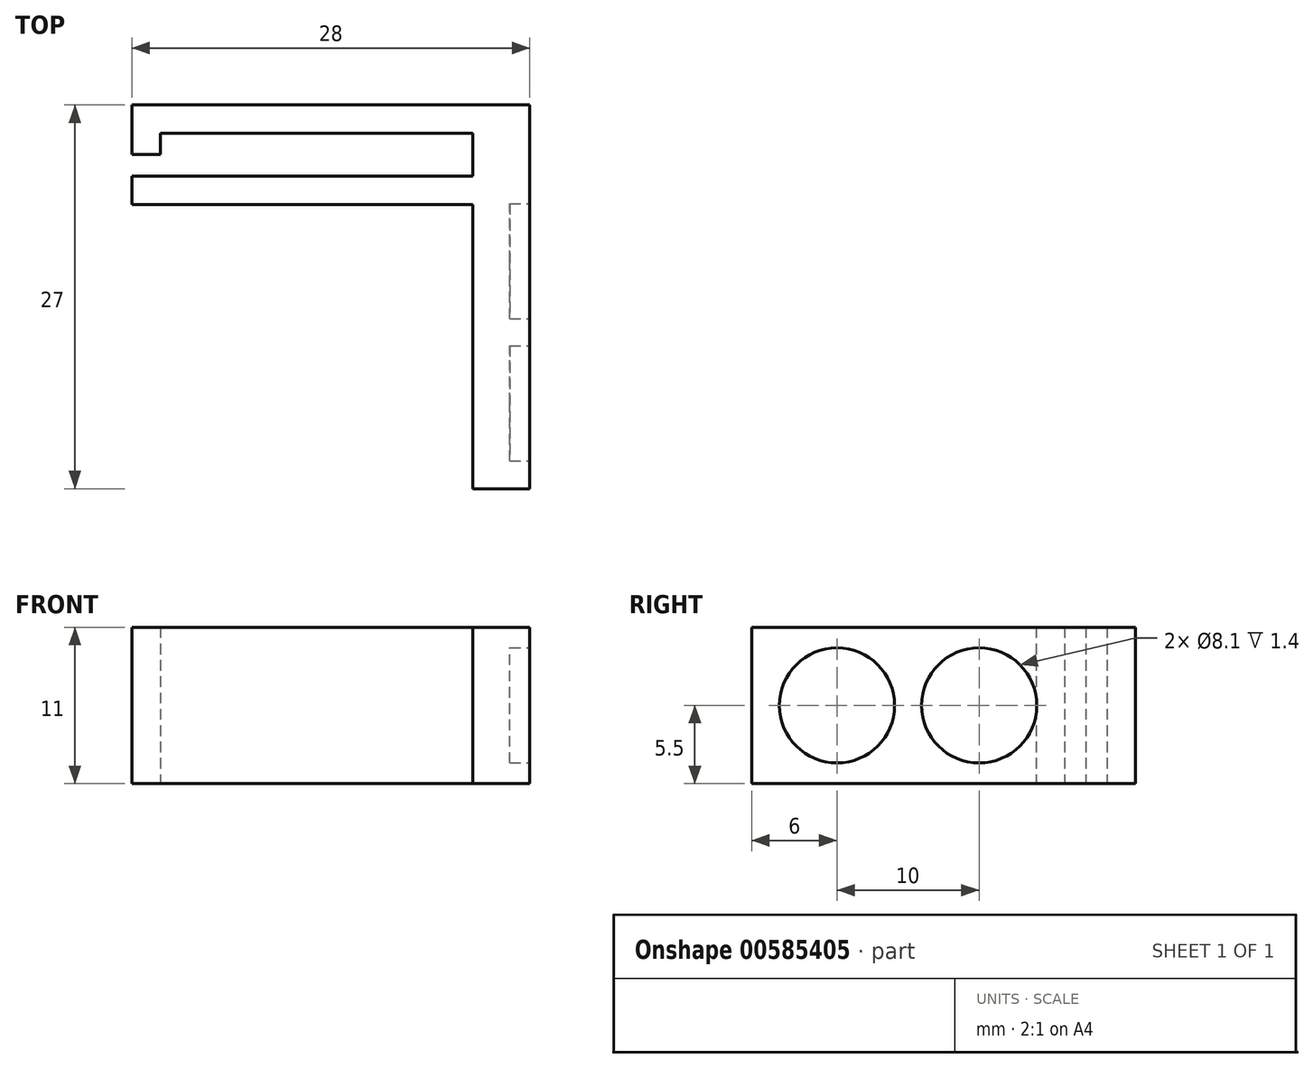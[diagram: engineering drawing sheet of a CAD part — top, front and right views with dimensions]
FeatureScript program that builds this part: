
annotation { "Feature Type Name" : "Feature", "Feature Type Description" : "" }
export const myFeature = defineFeature(function(context is Context, id is Id, definition is map)
    precondition{}
    {
        {
            var Q0;
            Q0=qCreatedBy(makeId("Top.planeOp"),FACE);
            var sketch = newSketch(context, id + "F0", { "sketchPlane" : qUnion([Q0])});
            skLineSegment(sketch, "E0", {"start": v(0, 0) * mm, "end": v(0, -27) * mm});
            skLineSegment(sketch, "E1", {"start": v(0, -27) * mm, "end": v(-4, -27) * mm});
            skLineSegment(sketch, "E2", {"start": v(-4, -27) * mm, "end": v(-4, -7) * mm});
            skLineSegment(sketch, "E3", {"start": v(-4, -7) * mm, "end": v(-28, -7) * mm});
            skLineSegment(sketch, "E4", {"start": v(-28, -7) * mm, "end": v(-28, -5) * mm});
            skLineSegment(sketch, "E5", {"start": v(-28, -5) * mm, "end": v(-4, -5) * mm});
            skLineSegment(sketch, "E6", {"start": v(-4, -5) * mm, "end": v(-4, -2) * mm});
            skLineSegment(sketch, "E7", {"start": v(-4, -2) * mm, "end": v(-26, -2) * mm});
            skLineSegment(sketch, "E8", {"start": v(-26, -2) * mm, "end": v(-26, -3.5) * mm});
            skLineSegment(sketch, "E9", {"start": v(-26, -3.5) * mm, "end": v(-28, -3.5) * mm});
            skLineSegment(sketch, "E10", {"start": v(-28, -3.5) * mm, "end": v(-28, 0) * mm});
            skLineSegment(sketch, "E11", {"start": v(-28, 0) * mm, "end": v(0, 0) * mm});
            skSolve(sketch);
        }
        {
            var Q0;
            Q0 = qSketchRegion(id + "F0", true);
            extrude(context, id + "F1", {"entities" : qUnion([Q0]), "depth" : (8 + 3) * mm, "offsetDistance" : 25 * mm});
        }
        {
            var Q0;
            Q0=makeQuery(id+"F1.opExtrude","SWEPT_FACE",FACE,{"disambiguationData":[OSD([sQuery(id+"F0.wireOp",EDGE,"E0")])]});
            var sketch = newSketch(context, id + "F2", { "sketchPlane" : qUnion([Q0])});
            skLineSegment(sketch, "E12", {"start": v(-27, 5.5) * mm, "end": v(0, 5.5) * mm, "construction": true});
            skCircle(sketch, "E13", {"center": v(-21, 5.5) * mm, "radius": 4.05 * mm});
            skCircle(sketch, "E14", {"center": v(-11, 5.5) * mm, "radius": 4.05 * mm});
            skSolve(sketch);
        }
        {
            var Q0;
            Q0 = qSketchRegion(id + "F2", true);
            extrude(context, id + "F3", {"entities" : qUnion([Q0]), "operationType" : NewBodyOperationType.REMOVE, "oppositeDirection" : true, "depth" : 1.4 * mm, "offsetDistance" : 25 * mm});
        }
    });
